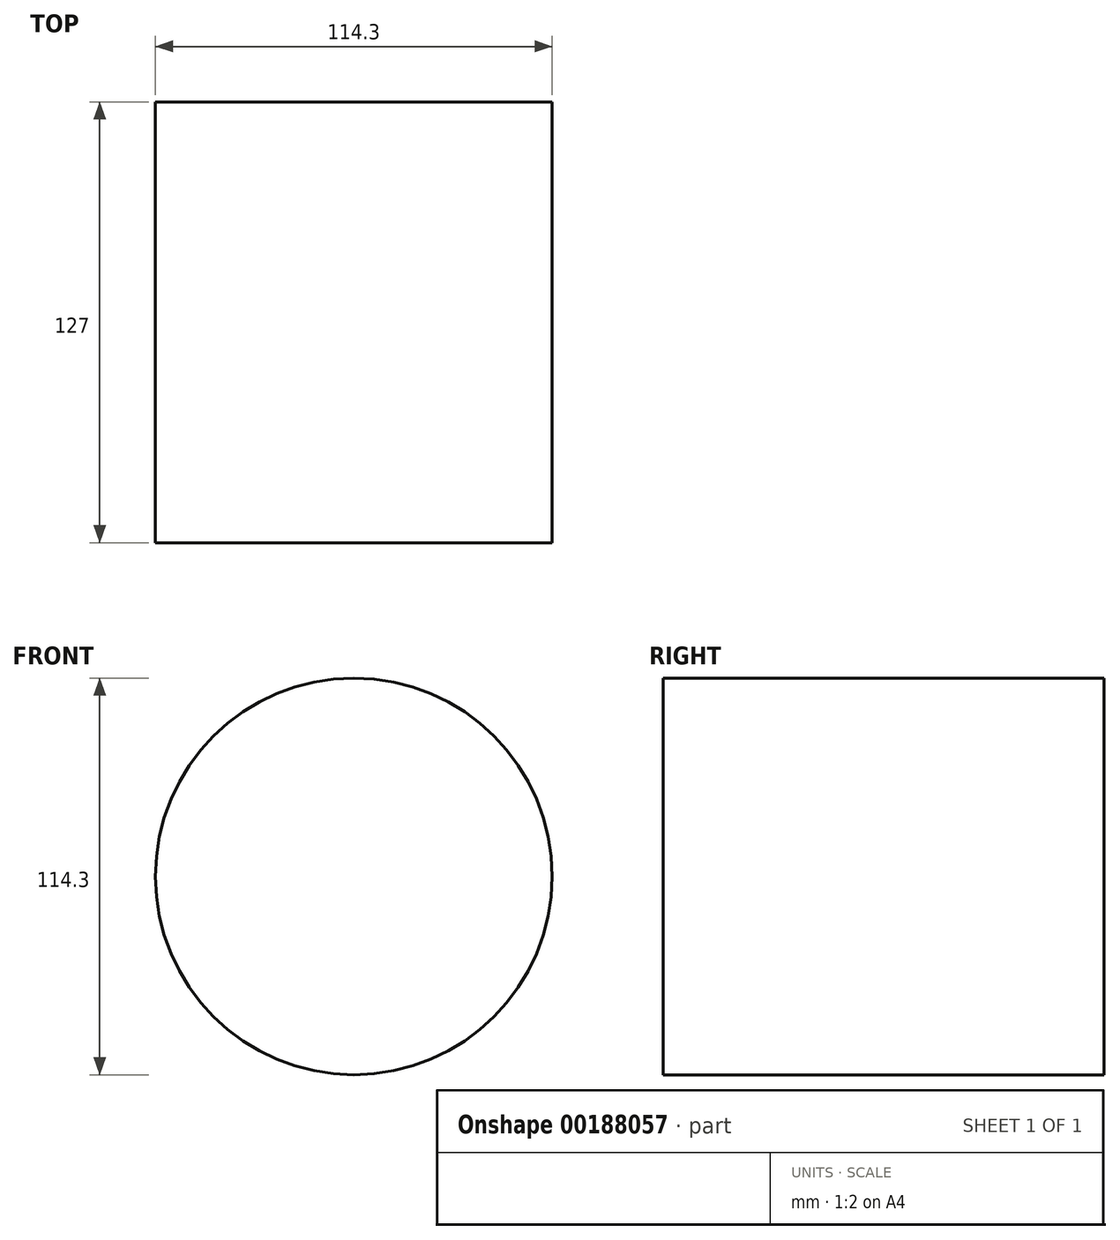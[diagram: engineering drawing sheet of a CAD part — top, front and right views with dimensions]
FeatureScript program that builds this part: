
annotation { "Feature Type Name" : "Feature", "Feature Type Description" : "" }
export const myFeature = defineFeature(function(context is Context, id is Id, definition is map)
    precondition{}
    {
        {
            var Q0;
            Q0=qCreatedBy(makeId("Front.planeOp"),FACE);
            var sketch = newSketch(context, id + "F0", { "sketchPlane" : qUnion([Q0])});
            skCircle(sketch, "E0", {"center": v(-0.21, 0.17) * mm, "radius": 57.15 * mm});
            skSolve(sketch);
        }
        {
            var Q0;
            Q0=makeQuery(id+"F0.imprint","IMPRINT",FACE,{"disambiguationData":[TD([[makeQuery(id+"F0.imprint","IMPRINT",EDGE,{"derivedFrom":sQuery(id+"F0.wireOp",EDGE,"E0")}),1.0]])]});
            extrude(context, id + "F1", {"entities" : qUnion([Q0]), "depth" : 127 * mm});
        }
    });
